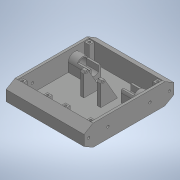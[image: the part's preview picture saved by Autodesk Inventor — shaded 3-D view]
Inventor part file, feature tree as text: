
AUTODESK INVENTOR PART (.ipt)
format: ipt  version: 2020 (Build 240168000, 168)  size: 379,904 bytes
history: native  units: in
note: dims shown in document units (in); Inventor stores cm internally (conversion verified against a paired STEP export)
features: projected_geometry x13, extrude x11, sketch x11, mirror x4, plane x1
ambient origin geometry x8: Origin, YZ Plane, XZ Plane, XY Plane, X Axis, Y Axis, Z Axis, Center Point
bodies: Solid1 (feature_tree)
feature tree (40):
  extrude  "Extrusion1"  Depth=5.9055in
  extrude  "Extrusion2"  TaperAngle=0.0deg  [1 undecoded]
  extrude  "Extrusion3"  Depth=1.2598in
  extrude  "Extrusion4"  Depth=0.315in
  extrude  "Extrusion5"  TaperAngle=0.0deg  [1 undecoded]
  extrude  "Extrusion6"  Depth=0.689in
  mirror  "Mirror1"
  extrude  "Extrusion7"  Depth=0.0787in
  mirror  "Mirror2"
  extrude  "Extrusion8"  Depth=0.5512in
  mirror  "Mirror3"
  plane  "Work Plane1"
  extrude  "Extrusion9"  Depth=0.7874in TaperAngle=0.0deg
  mirror  "Mirror4"
  extrude  "Extrusion10"  Depth=6.063in TaperAngle=0.0deg
  extrude  "Extrusion11"  Depth=0.1575in
  sketch  "Sketch1"  dims[d0=1.378in d1=5.9055in]
  sketch  "Sketch2"  dims[d2=5.1181in d3=0.0in]
  projected_geometry  "Projected Loop1"
  sketch  "Sketch3"  dims[d4=0.1575in d5=1.2598in]
  projected_geometry  "Projected Loop2"
  projected_geometry  "Projected Loop3"
  sketch  "Sketch4"  dims[d6=0.0in d8=0.315in]
  sketch  "Sketch5"  dims[d10=1.1898in d11=0.0in]
  projected_geometry  "Projected Loop4"
  sketch  "Sketch6"  dims[d12=0.6496in d13=0.689in]
  sketch  "Sketch7"  dims[d14=1.5748in d15=0.0787in]
  sketch  "Sketch9"  dims[d16=0.5512in d17=0.0in d18=0.6102in]
  sketch  "Sketch10"  dims[d19=0.4803in d20=0.7874in d21=0.0in]
  sketch  "Sketch12"  dims[d22=0.1654in d23=6.063in d24=0.0in]
  projected_geometry  "Projected Loop6"
  projected_geometry  "Projected Loop7"
  projected_geometry  "Projected Loop8"
  sketch  "Sketch13"  dims[d25=0.5967in d26=0.1575in d27=1.5748in d28=0.0in d29=0.0in d30=0.1575in d31=0.2756in d32=0.0in d33=0.4331in d34=0.122in d38=2.7559in d40=0.061in d41=0.0909in d42=0.2362in d43=0.0in d44=60.0deg d45=0.0787in d46=0.315in d48=1.1898in d49=0.0in d51=0.1575in d52=0.1575in d53=0.2756in d54=0.0in]
  projected_geometry  "Projected Loop9"
  projected_geometry  "Projected Loop10"
  projected_geometry  "Projected Loop11"
  projected_geometry  "Projected Loop12"
  projected_geometry  "Projected Loop13"
  projected_geometry  "Projected Loop14"
note: 2 required parameter values undecoded (feature->parameter linkage not recoverable at this tier; creation-order binding heuristic only, values carry confidence <= 0.55)
